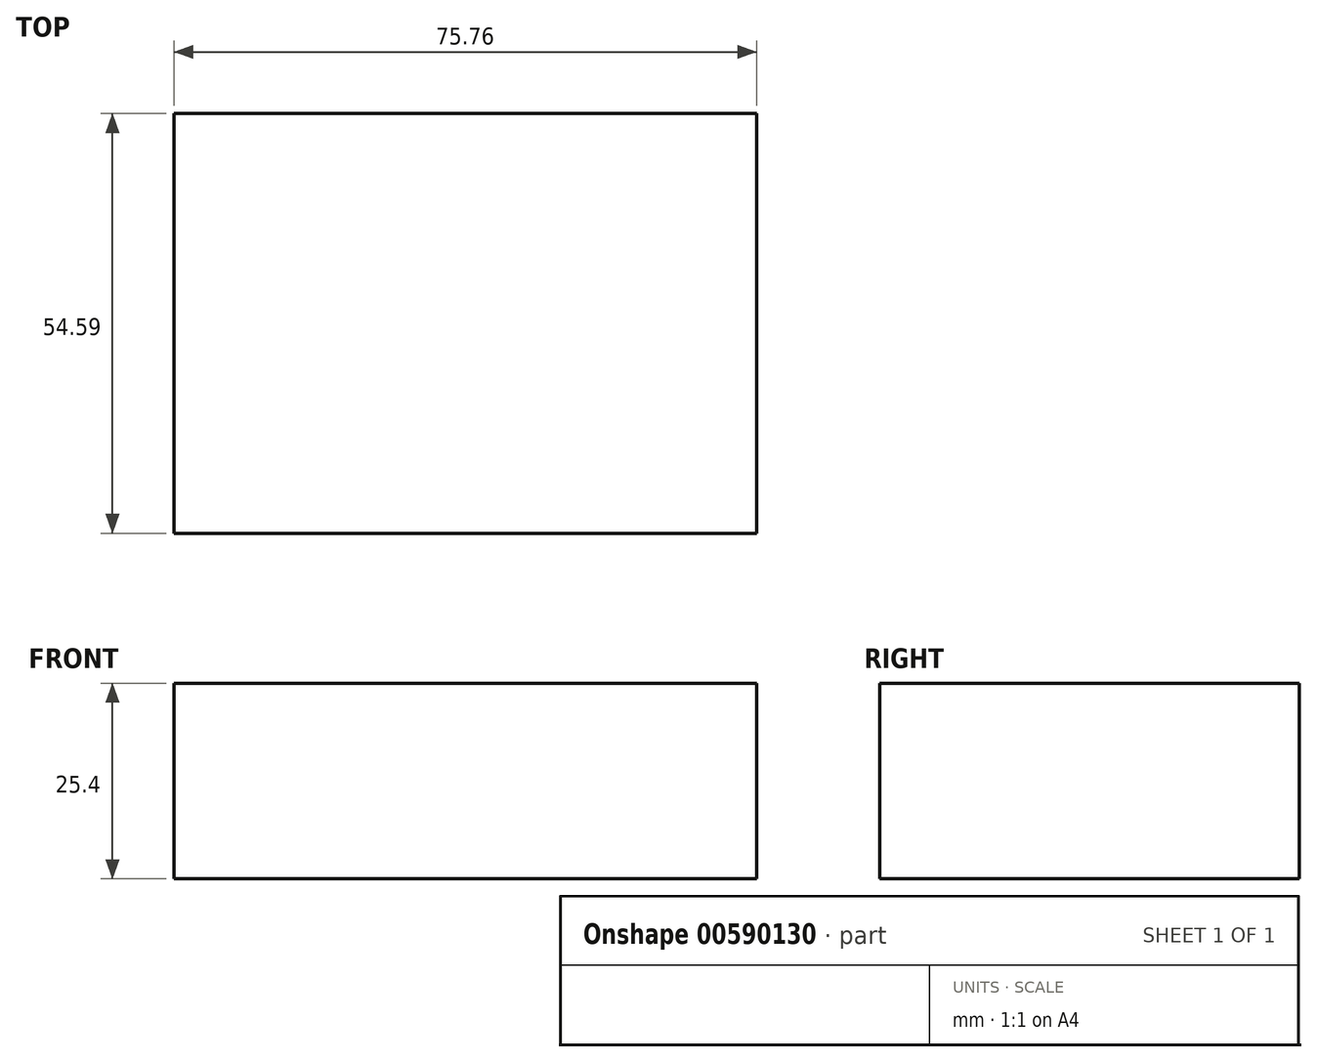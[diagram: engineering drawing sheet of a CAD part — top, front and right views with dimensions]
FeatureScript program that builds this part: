
annotation { "Feature Type Name" : "Feature", "Feature Type Description" : "" }
export const myFeature = defineFeature(function(context is Context, id is Id, definition is map)
    precondition{}
    {
        {
            var Q0;
            Q0=qCreatedBy(makeId("Top.planeOp"),FACE);
            var sketch = newSketch(context, id + "F0", { "sketchPlane" : qUnion([Q0])});
            skLineSegment(sketch, "E0.bottom", {"start": v(-38.8, 25.12) * mm, "end": v(36.95, 25.12) * mm});
            skLineSegment(sketch, "E0.top", {"start": v(-38.8, -29.47) * mm, "end": v(36.95, -29.47) * mm});
            skLineSegment(sketch, "E0.left", {"start": v(-38.8, 25.12) * mm, "end": v(-38.8, -29.47) * mm});
            skLineSegment(sketch, "E0.right", {"start": v(36.95, 25.12) * mm, "end": v(36.95, -29.47) * mm});
            skSolve(sketch);
        }
        {
            var Q0;
            Q0 = qSketchRegion(id + "F0", true);
            extrude(context, id + "F1", {"entities" : qUnion([Q0]), "depth" : 25.4 * mm, "offsetDistance" : 25.4 * mm});
        }
    });
